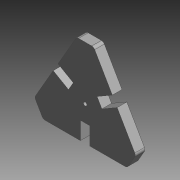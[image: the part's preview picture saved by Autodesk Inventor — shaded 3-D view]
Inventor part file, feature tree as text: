
AUTODESK INVENTOR PART (.ipt)
format: ipt  version: 2014 SP1 (Build 180222100, 222)  size: 117,248 bytes
history: native  units: in
note: dims shown in document units (in); Inventor stores cm internally (conversion verified against a paired STEP export)
features: extrude x2, sketch x2, pattern_circular x1, chamfer x1, fillet x1
ambient origin geometry x8: Origin, YZ Plane, XZ Plane, XY Plane, X Axis, Y Axis, Z Axis, Center Point
bodies: Solid1 (feature_tree)
feature tree (7):
  extrude  "Extrusion1"  Depth=0.0787in
  extrude  "Extrusion2"  Depth=0.4071in TaperAngle=0.0deg
  pattern_circular  "Circular Pattern1"  Count=3 Angle=360.0deg
  chamfer  "Chamfer1"  Distance=0.3937in Angle=45.0deg
  fillet  "Fillet1"  Radius=0.0787in
  sketch  "Sketch1"  dims[d0=0.0787in d1=0.7874in]
  sketch  "Sketch2"  dims[d2=0.2228in d3=0.0in d6=0.3396in d7=0.0in d8=1.1811in d9=360.0deg d11=0.3937in d12=0.0787in d13=45.0deg d14=0.0787in d15=0.4071in d16=0.1114in d17=0.1114in]
